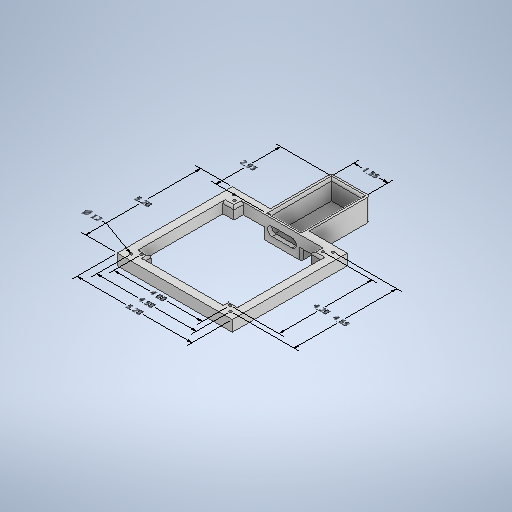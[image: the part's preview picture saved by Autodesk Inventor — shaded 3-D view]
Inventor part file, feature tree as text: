
AUTODESK INVENTOR PART (.ipt)
format: ipt  version: 2025.2 (Build 292293000, 293)  size: 426,496 bytes
history: native  units: in
note: dims shown in document units (in); Inventor stores cm internally (conversion verified against a paired STEP export)
features: other x10, extrude x8, thread x8, sketch x8, fillet x1
ambient origin geometry x8: Origin, YZ Plane, XZ Plane, XY Plane, X Axis, Y Axis, Z Axis, Center Point
bodies: Solid1 (feature_tree)
feature tree (35):
  other  "Annotations"
  extrude  "Extrusion1"  Depth=5.2in
  extrude  "Extrusion2"  Depth=4.5in
  thread  "Thread1"  [1 undecoded]
  thread  "Thread2"  [1 undecoded]
  thread  "Thread3"  [1 undecoded]
  thread  "Thread4"  [1 undecoded]
  extrude  "Extrusion3"  Depth=4.5in
  thread  "Thread5"  [1 undecoded]
  thread  "Thread6"  [1 undecoded]
  thread  "Thread7"  [1 undecoded]
  thread  "Thread8"  [1 undecoded]
  extrude  "Extrusion4"  Depth=0.12in
  extrude  "Extrusion5"  Depth=1.0in TaperAngle=0.0deg
  extrude  "Extrusion6"  Depth=0.5in TaperAngle=0.0deg
  extrude  "Extrusion8"  Depth=0.5in TaperAngle=0.0deg
  fillet  "Fillet3"  Radius=0.12in
  extrude  "Extrusion9"  Depth=5.2in
  sketch  "Sketch1"  dims[d0=5.2in d1=5.2in]
  sketch  "Sketch2"  dims[d2=2.6in d3=2.6in d4=0.5in d5=0.0in d7=4.65in d8=4.5in d9=0.0in]
  sketch  "Sketch3"  dims[d10=4.65in d11=4.5in d12=0.35in d14=0.35in d15=0.275in d16=0.12in]
  sketch  "Sketch4"  dims[d17=0.12in d18=0.12in]
  sketch  "Sketch5"  dims[d19=0.12in d20=1.0in d21=0.0in]
  sketch  "Sketch6"  dims[d22=0.5in d23=0.0in d24=0.5in d25=0.0in]
  sketch  "Sketch8"  dims[d26=0.5in d27=0.0in d28=0.5in d29=0.0in d30=0.12in]
  sketch  "Sketch9"  dims[d31=0.12in d32=0.12in d33=0.12in d34=4.0in d35=4.0in d36=4.2in d37=4.2in d38=0.0in d39=0.0in d40=0.6in d41=0.5in d42=1.0in d43=0.0in d44=0.5in d45=0.0in d46=0.5in d47=0.0in d48=0.5in d49=0.0in d50=0.5in d51=0.0in d52=4.5in d53=3.75in d54=2.25in d55=3.5in d56=4.5in d57=0.35in d58=1.0in d59=0.0in d60=1.75in d61=1.725in d62=2.75in d63=0.0in d64=1.75in d65=1.0in d66=0.0in d74=1.35in d75=2.725in d76=0.2in d77=0.1875in d78=0.875in d79=0.0in d80=0.1in d81=0.4in d82=0.0in d83=0.45in d84=0.875in d85=0.0in d100=0.0403in d101=0.032in d102=4.65in d103=0.0514in d104=4.2in d105=0.0617in d106=0.0488in d107=4.0in d108=4.5in d86=0.0in d87=0.3937in d88=1.55in d89=0.0in d90=0.3937in d91=2.925in d92=0.1583in d93=0.12in d94=0.0in d95=0.3937in d96=5.2in d97=0.0in d98=0.3937in d99=5.2in]
  other  "Linear Dimension 1"
  other  "Linear Dimension 2"
  other  "Diameter Dimension 1"
  other  "Linear Dimension 3"
  other  "Linear Dimension 4"
  other  "Linear Dimension 5"
  other  "Linear Dimension 6"
  other  "Linear Dimension 7"
  other  "Linear Dimension 8"
note: 8 required parameter values undecoded (feature->parameter linkage not recoverable at this tier; creation-order binding heuristic only, values carry confidence <= 0.55)
